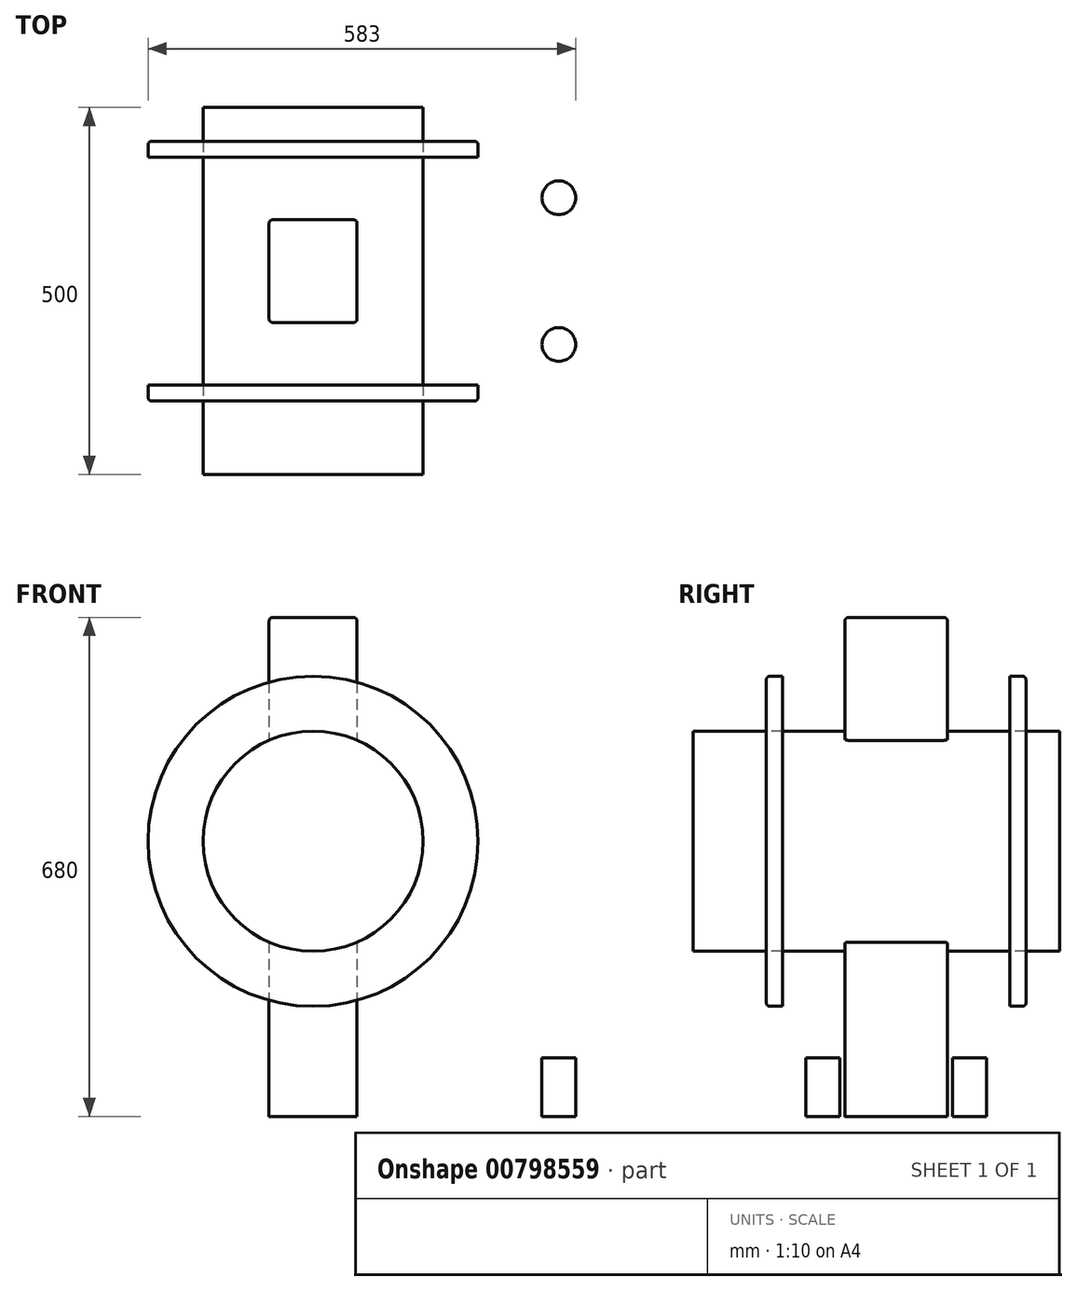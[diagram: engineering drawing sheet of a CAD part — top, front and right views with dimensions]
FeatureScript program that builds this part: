
annotation { "Feature Type Name" : "Feature", "Feature Type Description" : "" }
export const myFeature = defineFeature(function(context is Context, id is Id, definition is map)
    precondition{}
    {
        {
            var Q0;
            Q0=qCreatedBy(makeId("Front.planeOp"),FACE);
            var sketch = newSketch(context, id + "F0", { "sketchPlane" : qUnion([Q0])});
            skCircle(sketch, "E0", {"center": v(0, 0) * mm, "radius": 150 * mm});
            skLineSegment(sketch, "E1.bottom", {"start": v(0, 0) * mm, "end": v(-285, 0) * mm});
            skLineSegment(sketch, "E1.top", {"start": v(0, -375) * mm, "end": v(-400, -375) * mm});
            skLineSegment(sketch, "E1.left", {"start": v(0, 0) * mm, "end": v(0, -375) * mm});
            skLineSegment(sketch, "E1.right", {"start": v(-400, -295) * mm, "end": v(-400, -375) * mm});
            skLineSegment(sketch, "E2.bottom", {"start": v(0, 0) * mm, "end": v(285, 0) * mm});
            skLineSegment(sketch, "E2.top", {"start": v(0, -375) * mm, "end": v(400, -375) * mm});
            skLineSegment(sketch, "E2.right", {"start": v(400, -295) * mm, "end": v(400, -375) * mm});
            skCircle(sketch, "E3", {"center": v(0, 0) * mm, "radius": 200 * mm});
            skLineSegment(sketch, "E4", {"start": v(-285, 0) * mm, "end": v(-285, -295) * mm});
            skLineSegment(sketch, "E5", {"start": v(-285, -295) * mm, "end": v(-400, -295) * mm});
            skLineSegment(sketch, "E6", {"start": v(285, 0) * mm, "end": v(285, -295) * mm});
            skLineSegment(sketch, "E7", {"start": v(285, -295) * mm, "end": v(400, -295) * mm});
            skArc(sketch, "E8", {"start": v(285, 0) * mm, "mid": v(0, 275) * mm, "end": v(-285, 0) * mm});
            skSolve(sketch);
        }
        {
            var Q0;
            {var subQ1=sQuery(id+"F0.wireOp",EDGE,"E2.top");Q0=makeQuery(id+"F0.imprint","IMPRINT",FACE,{"disambiguationData":[TD([[makeQuery(id+"F0.imprint","IMPRINT",EDGE,{"derivedFrom":subQ1}),1.0]])]});}
            var Q1;
            {var subQ0=sQuery(id+"F0.wireOp",EDGE,"E8");Q1=makeQuery(id+"F0.imprint","IMPRINT",FACE,{"disambiguationData":[TD([[makeQuery(id+"F0.imprint","IMPRINT",EDGE,{"derivedFrom":subQ0}),1.0]])]});}
            var Q2;
            {var subQ0=sQuery(id+"F0.wireOp",EDGE,"E1.bottom");var subQ1=sQuery(id+"F0.wireOp",EDGE,"E0");var subQ2=makeQuery(id+"F0.imprint","INTERSECT",VERTEX,{"derivedFrom":[subQ1,subQ0]});Q2=makeQuery(id+"F0.imprint","IMPRINT",FACE,{"disambiguationData":[TD([[makeQuery(id+"F0.imprint","IMPRINT",EDGE,{"disambiguationData":[TD([[subQ2,1.0]])],"derivedFrom":subQ1}),-1.0]])]});}
            var Q3;
            {var subQ1=sQuery(id+"F0.wireOp",EDGE,"E1.top");Q3=makeQuery(id+"F0.imprint","IMPRINT",FACE,{"disambiguationData":[TD([[makeQuery(id+"F0.imprint","IMPRINT",EDGE,{"derivedFrom":subQ1}),-1.0]])]});}
            var Q4;
            {var subQ0=sQuery(id+"F0.wireOp",EDGE,"E1.bottom");var subQ1=sQuery(id+"F0.wireOp",EDGE,"E0");var subQ2=makeQuery(id+"F0.imprint","INTERSECT",VERTEX,{"derivedFrom":[subQ1,subQ0]});Q4=makeQuery(id+"F0.imprint","IMPRINT",FACE,{"disambiguationData":[TD([[makeQuery(id+"F0.imprint","IMPRINT",EDGE,{"disambiguationData":[TD([[subQ2,-1.0]])],"derivedFrom":subQ1}),-1.0]])]});}
            var Q5;
            {var subQ0=sQuery(id+"F0.wireOp",EDGE,"E2.bottom");var subQ1=sQuery(id+"F0.wireOp",EDGE,"E0");var subQ2=makeQuery(id+"F0.imprint","INTERSECT",VERTEX,{"derivedFrom":[subQ1,subQ0]});Q5=makeQuery(id+"F0.imprint","IMPRINT",FACE,{"disambiguationData":[TD([[makeQuery(id+"F0.imprint","IMPRINT",EDGE,{"disambiguationData":[TD([[subQ2,1.0]])],"derivedFrom":subQ1}),-1.0]])]});}
            var Q6;
            {var subQ0=sQuery(id+"F0.wireOp",EDGE,"E2.bottom");var subQ1=sQuery(id+"F0.wireOp",EDGE,"E0");var subQ2=makeQuery(id+"F0.imprint","INTERSECT",VERTEX,{"derivedFrom":[subQ1,subQ0]});Q6=makeQuery(id+"F0.imprint","IMPRINT",FACE,{"disambiguationData":[TD([[makeQuery(id+"F0.imprint","IMPRINT",EDGE,{"disambiguationData":[TD([[subQ2,1.0]])],"derivedFrom":subQ1}),1.0]])]});}
            var Q7;
            {var subQ0=sQuery(id+"F0.wireOp",EDGE,"E1.bottom");var subQ1=sQuery(id+"F0.wireOp",EDGE,"E0");var subQ2=makeQuery(id+"F0.imprint","INTERSECT",VERTEX,{"derivedFrom":[subQ1,subQ0]});Q7=makeQuery(id+"F0.imprint","IMPRINT",FACE,{"disambiguationData":[TD([[makeQuery(id+"F0.imprint","IMPRINT",EDGE,{"disambiguationData":[TD([[subQ2,-1.0]])],"derivedFrom":subQ1}),1.0]])]});}
            var Q8;
            {var subQ0=sQuery(id+"F0.wireOp",EDGE,"E1.bottom");var subQ1=sQuery(id+"F0.wireOp",EDGE,"E0");var subQ2=makeQuery(id+"F0.imprint","INTERSECT",VERTEX,{"derivedFrom":[subQ1,subQ0]});Q8=makeQuery(id+"F0.imprint","IMPRINT",FACE,{"disambiguationData":[TD([[makeQuery(id+"F0.imprint","IMPRINT",EDGE,{"disambiguationData":[TD([[subQ2,1.0]])],"derivedFrom":subQ1}),1.0]])]});}
            extrude(context, id + "F1", {"entities" : qUnion([Q0, Q1, Q2, Q3, Q4, Q5, Q6, Q7, Q8]), "depth" : 310 * mm, "offsetDistance" : 25 * mm});
        }
        {
            var Q0;
            Q0=makeQuery(id+"F1.opExtrude","CAP_FACE",FACE,{"disambiguationData":[OSD([sQuery(id+"F0.wireOp",EDGE,"E1.top"),sQuery(id+"F0.wireOp",EDGE,"E1.right"),sQuery(id+"F0.wireOp",EDGE,"E2.top"),sQuery(id+"F0.wireOp",EDGE,"E2.right"),sQuery(id+"F0.wireOp",EDGE,"E4"),sQuery(id+"F0.wireOp",EDGE,"E5"),sQuery(id+"F0.wireOp",EDGE,"E6"),sQuery(id+"F0.wireOp",EDGE,"E7"),sQuery(id+"F0.wireOp",EDGE,"E8")])],"isStart":true});
            var sketch = newSketch(context, id + "F2", { "sketchPlane" : qUnion([Q0])});
            skCircle(sketch, "E9", {"center": v(0, 0) * mm, "radius": 225 * mm});
            skSolve(sketch);
        }
        {
            var Q0;
            Q0=makeQuery(id+"F2.imprint","IMPRINT",FACE,{"disambiguationData":[TD([[makeQuery(id+"F2.imprint","IMPRINT",EDGE,{"derivedFrom":sQuery(id+"F2.wireOp",EDGE,"E9")}),1.0]])]});
            var Q1;
            Q1=sQuery(id+"F2.wireOp",EDGE,"E9");
            extrude(context, id + "F3", {"entities" : qUnion([Q0]), "surfaceEntities" : qUnion([Q1]), "depth" : 22 * mm, "offsetDistance" : 25 * mm});
        }
        {
            var Q0;
            Q0=makeQuery(id+"F1.opExtrude","CAP_FACE",FACE,{"disambiguationData":[OSD([sQuery(id+"F0.wireOp",EDGE,"E1.top"),sQuery(id+"F0.wireOp",EDGE,"E1.right"),sQuery(id+"F0.wireOp",EDGE,"E2.top"),sQuery(id+"F0.wireOp",EDGE,"E2.right"),sQuery(id+"F0.wireOp",EDGE,"E4"),sQuery(id+"F0.wireOp",EDGE,"E5"),sQuery(id+"F0.wireOp",EDGE,"E6"),sQuery(id+"F0.wireOp",EDGE,"E7"),sQuery(id+"F0.wireOp",EDGE,"E8")])],"isStart":false});
            var sketch = newSketch(context, id + "F4", { "sketchPlane" : qUnion([Q0])});
            skCircle(sketch, "E10", {"center": v(0, 0) * mm, "radius": 225 * mm});
            skSolve(sketch);
        }
        {
            var Q0;
            Q0=makeQuery(id+"F4.imprint","IMPRINT",FACE,{"disambiguationData":[TD([[makeQuery(id+"F4.imprint","IMPRINT",EDGE,{"derivedFrom":sQuery(id+"F4.wireOp",EDGE,"E10")}),1.0]])]});
            extrude(context, id + "F5", {"entities" : qUnion([Q0]), "operationType" : NewBodyOperationType.ADD, "depth" : 22 * mm, "offsetDistance" : 25 * mm});
        }
        {
            var Q0;
            Q0=makeQuery(id+"F1.opExtrude","SWEPT_FACE",FACE,{"disambiguationData":[OSD([sQuery(id+"F0.wireOp",EDGE,"E1.top"),sQuery(id+"F0.wireOp",EDGE,"E2.top")])]});
            var sketch = newSketch(context, id + "F6", { "sketchPlane" : qUnion([Q0])});
            skLineSegment(sketch, "E11", {"start": v(-400, 155) * mm, "end": v(400, 155) * mm, "construction": true});
            skCircle(sketch, "E12", {"center": v(-335, 55) * mm, "radius": 23 * mm});
            skCircle(sketch, "E13", {"center": v(-335, 255) * mm, "radius": 23 * mm});
            skLineSegment(sketch, "E14", {"start": v(0, 0) * mm, "end": v(0, 310) * mm, "construction": true});
            skCircle(sketch, "E15.MirrorC", {"center": v(335, 55) * mm, "radius": 23 * mm});
            skCircle(sketch, "E16.MirrorC", {"center": v(335, 255) * mm, "radius": 23 * mm});
            skSolve(sketch);
        }
        {
            var Q0;
            Q0=makeQuery(id+"F6.imprint","IMPRINT",FACE,{"disambiguationData":[TD([[makeQuery(id+"F6.imprint","IMPRINT",EDGE,{"derivedFrom":sQuery(id+"F6.wireOp",EDGE,"E13")}),1.0]])]});
            var Q1;
            Q1=makeQuery(id+"F6.imprint","IMPRINT",FACE,{"disambiguationData":[TD([[makeQuery(id+"F6.imprint","IMPRINT",EDGE,{"derivedFrom":sQuery(id+"F6.wireOp",EDGE,"E12")}),1.0]])]});
            var Q2;
            Q2=makeQuery(id+"F6.imprint","IMPRINT",FACE,{"disambiguationData":[TD([[makeQuery(id+"F6.imprint","IMPRINT",EDGE,{"derivedFrom":sQuery(id+"F6.wireOp",EDGE,"E15.MirrorC")}),-1.0]])]});
            var Q3;
            Q3=makeQuery(id+"F6.imprint","IMPRINT",FACE,{"disambiguationData":[TD([[makeQuery(id+"F6.imprint","IMPRINT",EDGE,{"derivedFrom":sQuery(id+"F6.wireOp",EDGE,"E16.MirrorC")}),-1.0]])]});
            extrude(context, id + "F7", {"entities" : qUnion([Q0, Q1, Q2, Q3]), "operationType" : NewBodyOperationType.REMOVE, "endBound" : BoundingType.THROUGH_ALL, "oppositeDirection" : true, "depth" : 25 * mm, "offsetDistance" : 25 * mm});
        }
        {
            var Q0;
            Q0=makeQuery(id+"F1.opExtrude","CAP_EDGE",EDGE,{"disambiguationData":[OSD([sQuery(id+"F0.wireOp",EDGE,"E1.right")])],"isStart":true});
            var Q1;
            Q1=makeQuery(id+"F1.opExtrude","CAP_EDGE",EDGE,{"disambiguationData":[OSD([sQuery(id+"F0.wireOp",EDGE,"E1.right")])],"isStart":false});
            var Q2;
            Q2=makeQuery(id+"F1.opExtrude","SWEPT_EDGE",EDGE,{"disambiguationData":[OSD([sQuery(id+"F0.wireOp",EDGE,"E1.right"),sQuery(id+"F0.wireOp",EDGE,"E5")])]});
            var Q3;
            Q3=makeQuery(id+"F1.opExtrude","CAP_EDGE",EDGE,{"disambiguationData":[OSD([sQuery(id+"F0.wireOp",EDGE,"E4")])],"isStart":true});
            var Q4;
            Q4=makeQuery(id+"F1.opExtrude","CAP_EDGE",EDGE,{"disambiguationData":[OSD([sQuery(id+"F0.wireOp",EDGE,"E5")])],"isStart":true});
            var Q5;
            Q5=makeQuery(id+"F1.opExtrude","CAP_EDGE",EDGE,{"disambiguationData":[OSD([sQuery(id+"F0.wireOp",EDGE,"E4")])],"isStart":false});
            var Q6;
            Q6=makeQuery(id+"F1.opExtrude","CAP_EDGE",EDGE,{"disambiguationData":[OSD([sQuery(id+"F0.wireOp",EDGE,"E5")])],"isStart":false});
            var Q7;
            Q7=makeQuery(id+"F1.opExtrude","CAP_EDGE",EDGE,{"disambiguationData":[OSD([sQuery(id+"F0.wireOp",EDGE,"E8")])],"isStart":true});
            var Q8;
            Q8=makeQuery(id+"F1.opExtrude","CAP_EDGE",EDGE,{"disambiguationData":[OSD([sQuery(id+"F0.wireOp",EDGE,"E8")])],"isStart":false});
            var Q9;
            Q9=makeQuery(id+"F1.opExtrude","CAP_EDGE",EDGE,{"disambiguationData":[OSD([sQuery(id+"F0.wireOp",EDGE,"E6")])],"isStart":true});
            var Q10;
            Q10=makeQuery(id+"F1.opExtrude","CAP_EDGE",EDGE,{"disambiguationData":[OSD([sQuery(id+"F0.wireOp",EDGE,"E7")])],"isStart":true});
            var Q11;
            Q11=makeQuery(id+"F1.opExtrude","CAP_EDGE",EDGE,{"disambiguationData":[OSD([sQuery(id+"F0.wireOp",EDGE,"E2.right")])],"isStart":true});
            var Q12;
            Q12=makeQuery(id+"F1.opExtrude","SWEPT_EDGE",EDGE,{"disambiguationData":[OSD([sQuery(id+"F0.wireOp",EDGE,"E2.right"),sQuery(id+"F0.wireOp",EDGE,"E7")])]});
            var Q13;
            Q13=makeQuery(id+"F1.opExtrude","SWEPT_EDGE",EDGE,{"disambiguationData":[OSD([sQuery(id+"F0.wireOp",EDGE,"E6"),sQuery(id+"F0.wireOp",EDGE,"E7")])]});
            var Q14;
            Q14=makeQuery(id+"F1.opExtrude","CAP_EDGE",EDGE,{"disambiguationData":[OSD([sQuery(id+"F0.wireOp",EDGE,"E6")])],"isStart":false});
            var Q15;
            Q15=makeQuery(id+"F1.opExtrude","CAP_EDGE",EDGE,{"disambiguationData":[OSD([sQuery(id+"F0.wireOp",EDGE,"E7")])],"isStart":false});
            var Q16;
            Q16=makeQuery(id+"F1.opExtrude","CAP_EDGE",EDGE,{"disambiguationData":[OSD([sQuery(id+"F0.wireOp",EDGE,"E2.right")])],"isStart":false});
            var Q17;
            Q17=makeQuery(id+"F1.opExtrude","SWEPT_EDGE",EDGE,{"disambiguationData":[OSD([sQuery(id+"F0.wireOp",EDGE,"E4"),sQuery(id+"F0.wireOp",EDGE,"E5")])]});
            var Q18;
            Q18=makeQuery(id+"F3.opExtrude","CAP_EDGE",EDGE,{"disambiguationData":[OSD([sQuery(id+"F2.wireOp",EDGE,"E9")])],"isStart":false});
            var Q19;
            Q19=makeQuery(id+"F5.opExtrude","CAP_EDGE",EDGE,{"disambiguationData":[OSD([sQuery(id+"F4.wireOp",EDGE,"E10")])],"isStart":false});
            fillet(context, id + "F8", {"entities" : qUnion([Q0, Q1, Q2, Q3, Q4, Q5, Q6, Q7, Q8, Q9, Q10, Q11, Q12, Q13, Q14, Q15, Q16, Q17, Q18, Q19]), "radius" : 5 * mm, "tangentPropagation" : true, "allowEdgeOverflow" : false});
        }
        {
            var Q0;
            Q0=makeQuery(id+"F5.opExtrude","CAP_FACE",FACE,{"disambiguationData":[OSD([sQuery(id+"F4.wireOp",EDGE,"E10")])],"isStart":false});
            var sketch = newSketch(context, id + "F9", { "sketchPlane" : qUnion([Q0])});
            skCircle(sketch, "E17", {"center": v(0, 0) * mm, "radius": 150 * mm});
            skSolve(sketch);
        }
        {
            var Q0;
            Q0=makeQuery(id+"F9.imprint","IMPRINT",FACE,{"disambiguationData":[TD([[makeQuery(id+"F9.imprint","IMPRINT",EDGE,{"derivedFrom":sQuery(id+"F9.wireOp",EDGE,"E17")}),1.0]])]});
            extrude(context, id + "F10", {"entities" : qUnion([Q0]), "oppositeDirection" : true, "depth" : 400 * mm, "offsetDistance" : 25 * mm, "hasSecondDirection" : true, "secondDirectionOppositeDirection" : false, "secondDirectionDepth" : 100 * mm});
        }
        {
            var Q0;
            Q0=makeQuery(id+"F1.opExtrude","SWEPT_FACE",FACE,{"disambiguationData":[OSD([sQuery(id+"F0.wireOp",EDGE,"E1.top"),sQuery(id+"F0.wireOp",EDGE,"E2.top")])]});
            var sketch = newSketch(context, id + "F11", { "sketchPlane" : qUnion([Q0])});
            skLineSegment(sketch, "E18", {"start": v(0, 0) * mm, "end": v(0, 310) * mm});
            skLineSegment(sketch, "E19.bottom", {"start": v(-60, 225) * mm, "end": v(60, 225) * mm});
            skLineSegment(sketch, "E19.top", {"start": v(-60, 85) * mm, "end": v(60, 85) * mm});
            skLineSegment(sketch, "E19.left", {"start": v(-60, 225) * mm, "end": v(-60, 85) * mm});
            skLineSegment(sketch, "E19.right", {"start": v(60, 225) * mm, "end": v(60, 85) * mm});
            skPoint(sketch, "E19.middle", {"position": v(0, 155) * mm});
            skSolve(sketch);
        }
        {
            var Q0;
            {var subQ5=sQuery(id+"F11.wireOp",EDGE,"E19.right");Q0=makeQuery(id+"F11.imprint","IMPRINT",FACE,{"disambiguationData":[TD([[makeQuery(id+"F11.imprint","IMPRINT",EDGE,{"derivedFrom":subQ5}),-1.0]])]});}
            var Q1;
            {var subQ5=sQuery(id+"F11.wireOp",EDGE,"E19.left");Q1=makeQuery(id+"F11.imprint","IMPRINT",FACE,{"disambiguationData":[TD([[makeQuery(id+"F11.imprint","IMPRINT",EDGE,{"derivedFrom":subQ5}),1.0]])]});}
            extrude(context, id + "F12", {"entities" : qUnion([Q0, Q1]), "operationType" : NewBodyOperationType.ADD, "oppositeDirection" : true, "depth" : 680 * mm, "offsetDistance" : 25 * mm});
        }
        {
            var Q0;
            Q0=makeQuery(id+"F12.boolean.opBoolean","INTERSECT",EDGE,{"derivedFrom":[makeQuery(id+"F1.opExtrude","SWEPT_FACE",FACE,{"disambiguationData":[OSD([sQuery(id+"F0.wireOp",EDGE,"E8")])]}),makeQuery(id+"F12.opExtrude","SWEPT_FACE",FACE,{"disambiguationData":[OSD([sQuery(id+"F11.wireOp",EDGE,"E19.top")])]})]});
            var Q1;
            Q1=makeQuery(id+"F12.boolean.opBoolean","INTERSECT",EDGE,{"derivedFrom":[makeQuery(id+"F1.opExtrude","SWEPT_FACE",FACE,{"disambiguationData":[OSD([sQuery(id+"F0.wireOp",EDGE,"E8")])]}),makeQuery(id+"F12.opExtrude","SWEPT_FACE",FACE,{"disambiguationData":[OSD([sQuery(id+"F11.wireOp",EDGE,"E19.left")])]})]});
            var Q2;
            Q2=makeQuery(id+"F12.boolean.opBoolean","INTERSECT",EDGE,{"derivedFrom":[makeQuery(id+"F1.opExtrude","SWEPT_FACE",FACE,{"disambiguationData":[OSD([sQuery(id+"F0.wireOp",EDGE,"E8")])]}),makeQuery(id+"F12.opExtrude","SWEPT_FACE",FACE,{"disambiguationData":[OSD([sQuery(id+"F11.wireOp",EDGE,"E19.bottom")])]})]});
            var Q3;
            Q3=makeQuery(id+"F12.boolean.opBoolean","INTERSECT",EDGE,{"derivedFrom":[makeQuery(id+"F1.opExtrude","SWEPT_FACE",FACE,{"disambiguationData":[OSD([sQuery(id+"F0.wireOp",EDGE,"E8")])]}),makeQuery(id+"F12.opExtrude","SWEPT_FACE",FACE,{"disambiguationData":[OSD([sQuery(id+"F11.wireOp",EDGE,"E19.right")])]})]});
            var Q4;
            Q4=makeQuery(id+"F12.opExtrude","CAP_EDGE",EDGE,{"disambiguationData":[OSD([sQuery(id+"F11.wireOp",EDGE,"E19.left")])],"isStart":false});
            var Q5;
            Q5=makeQuery(id+"F12.opExtrude","CAP_EDGE",EDGE,{"disambiguationData":[OSD([sQuery(id+"F11.wireOp",EDGE,"E19.bottom")])],"isStart":false});
            var Q6;
            Q6=makeQuery(id+"F12.opExtrude","CAP_EDGE",EDGE,{"disambiguationData":[OSD([sQuery(id+"F11.wireOp",EDGE,"E19.right")])],"isStart":false});
            var Q7;
            Q7=makeQuery(id+"F12.opExtrude","SWEPT_EDGE",EDGE,{"disambiguationData":[OSD([sQuery(id+"F11.wireOp",EDGE,"E19.bottom"),sQuery(id+"F11.wireOp",EDGE,"E19.right")])]});
            var Q8;
            Q8=makeQuery(id+"F12.opExtrude","SWEPT_EDGE",EDGE,{"disambiguationData":[OSD([sQuery(id+"F11.wireOp",EDGE,"E19.bottom"),sQuery(id+"F11.wireOp",EDGE,"E19.left")])]});
            var Q9;
            Q9=makeQuery(id+"F12.opExtrude","SWEPT_EDGE",EDGE,{"disambiguationData":[OSD([sQuery(id+"F11.wireOp",EDGE,"E19.top"),sQuery(id+"F11.wireOp",EDGE,"E19.left")])]});
            var Q10;
            Q10=makeQuery(id+"F12.opExtrude","CAP_EDGE",EDGE,{"disambiguationData":[OSD([sQuery(id+"F11.wireOp",EDGE,"E19.top")])],"isStart":false});
            var Q11;
            Q11=makeQuery(id+"F12.opExtrude","SWEPT_EDGE",EDGE,{"disambiguationData":[OSD([sQuery(id+"F11.wireOp",EDGE,"E19.top"),sQuery(id+"F11.wireOp",EDGE,"E19.right")])]});
            fillet(context, id + "F13", {"entities" : qUnion([Q0, Q1, Q2, Q3, Q4, Q5, Q6, Q7, Q8, Q9, Q10, Q11]), "radius" : 5 * mm, "tangentPropagation" : true, "allowEdgeOverflow" : false});
        }
    });
